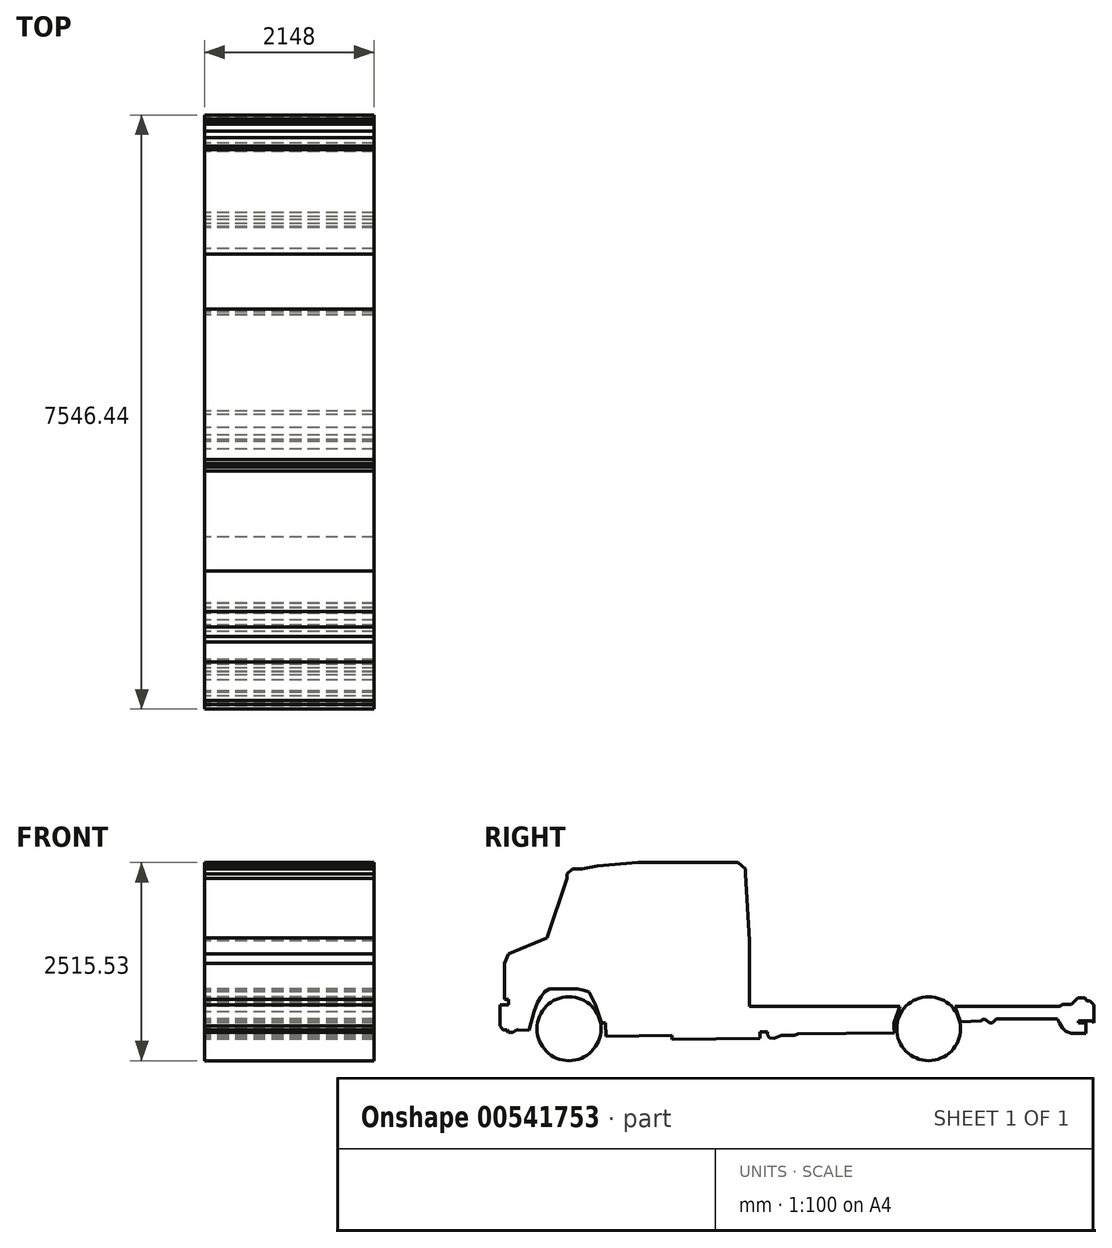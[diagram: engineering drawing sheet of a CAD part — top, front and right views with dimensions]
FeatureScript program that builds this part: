
annotation { "Feature Type Name" : "Feature", "Feature Type Description" : "" }
export const myFeature = defineFeature(function(context is Context, id is Id, definition is map)
    precondition{}
    {
        {
            var Q0;
            Q0=qCreatedBy(makeId("Right.planeOp"),FACE);
            var sketch = newSketch(context, id + "F0", { "sketchPlane" : qUnion([Q0])});
            skLineSegment(sketch, "E0", {"start": v(-5916.65, -35.76) * mm, "end": v(-5916.65, 86.1) * mm});
            skLineSegment(sketch, "E1", {"start": v(-5916.65, 86.1) * mm, "end": v(-5916.65, 228.27) * mm});
            skLineSegment(sketch, "E2", {"start": v(-5804.94, 228.27) * mm, "end": v(-5804.94, 299.36) * mm});
            skLineSegment(sketch, "E3", {"start": v(-5804.94, 299.36) * mm, "end": v(-5855.72, 299.36) * mm});
            skLineSegment(sketch, "E4", {"start": v(-5855.72, 299.36) * mm, "end": v(-5855.72, 664.94) * mm});
            skLineSegment(sketch, "E5", {"start": v(-5855.72, 664.94) * mm, "end": v(-5855.72, 756.33) * mm});
            skLineSegment(sketch, "E6", {"start": v(-5855.72, 756.33) * mm, "end": v(-5804.94, 878.2) * mm});
            skLineSegment(sketch, "E7", {"start": v(-5804.94, 878.2) * mm, "end": v(-5317.5, 1081.3) * mm});
            skLineSegment(sketch, "E8", {"start": v(-5317.5, 1081.3) * mm, "end": v(-5063.63, 1832.76) * mm});
            skLineSegment(sketch, "E9", {"start": v(-5063.63, 1832.76) * mm, "end": v(-5063.63, 1893.7) * mm});
            skLineSegment(sketch, "E10", {"start": v(-5063.63, 1893.7) * mm, "end": v(-4992.54, 1954.62) * mm});
            skLineSegment(sketch, "E11", {"start": v(-4992.54, 1954.62) * mm, "end": v(-4921.46, 1954.62) * mm});
            skLineSegment(sketch, "E12", {"start": v(-4921.46, 1954.62) * mm, "end": v(-4870.68, 1954.62) * mm});
            skLineSegment(sketch, "E13", {"start": v(-4870.68, 1954.62) * mm, "end": v(-4677.74, 1995.24) * mm});
            skLineSegment(sketch, "E14", {"start": v(-4677.74, 1995.24) * mm, "end": v(-4159.83, 2035.86) * mm});
            skLineSegment(sketch, "E15", {"start": v(-4159.83, 2035.86) * mm, "end": v(-2971.7, 2035.86) * mm});
            skLineSegment(sketch, "E16", {"start": v(-2971.7, 2035.86) * mm, "end": v(-2890.46, 2035.86) * mm});
            skLineSegment(sketch, "E17", {"start": v(-2890.46, 2035.86) * mm, "end": v(-2839.68, 1995.24) * mm});
            skLineSegment(sketch, "E18", {"start": v(-2839.68, 1995.24) * mm, "end": v(-2799.06, 1954.62) * mm});
            skLineSegment(sketch, "E19", {"start": v(-2799.06, 1954.62) * mm, "end": v(-2799.06, 1893.7) * mm});
            skLineSegment(sketch, "E20", {"start": v(-2799.06, 1893.7) * mm, "end": v(-2748.29, 1040.67) * mm});
            skLineSegment(sketch, "E21", {"start": v(-2748.29, 1040.67) * mm, "end": v(-2748.29, 675.1) * mm});
            skLineSegment(sketch, "E22", {"start": v(-2748.29, 675.1) * mm, "end": v(-2748.29, 228.27) * mm});
            skLineSegment(sketch, "E23", {"start": v(-2748.29, 228.27) * mm, "end": v(-2748.29, 210.87) * mm});
            skLineSegment(sketch, "E24", {"start": v(-2748.29, 210.87) * mm, "end": v(-832.65, 210.87) * mm});
            skLineSegment(sketch, "E25", {"start": v(-137.88, 210.87) * mm, "end": v(1193.96, 210.87) * mm});
            skLineSegment(sketch, "E26", {"start": v(1193.96, 210.87) * mm, "end": v(1235.52, 234.86) * mm});
            skLineSegment(sketch, "E27", {"start": v(1235.52, 234.86) * mm, "end": v(1346.42, 234.86) * mm});
            skLineSegment(sketch, "E28", {"start": v(1346.42, 234.86) * mm, "end": v(1427.07, 320.56) * mm});
            skLineSegment(sketch, "E29", {"start": v(1427.07, 320.56) * mm, "end": v(1512.77, 320.56) * mm});
            skLineSegment(sketch, "E30", {"start": v(1512.77, 320.56) * mm, "end": v(1543.24, 277.7) * mm});
            skPoint(sketch, "E30.endSnap0", {"position": v(1386.74, 277.7) * mm});
            skLineSegment(sketch, "E31", {"start": v(1543.24, 277.7) * mm, "end": v(1580.36, 277.7) * mm});
            skLineSegment(sketch, "E32", {"start": v(1580.36, 277.7) * mm, "end": v(1629.79, 231.19) * mm});
            skLineSegment(sketch, "E33", {"start": v(1629.79, 231.19) * mm, "end": v(1629.79, 210.87) * mm});
            skLineSegment(sketch, "E34", {"start": v(1629.79, 210.87) * mm, "end": v(1629.79, 0) * mm});
            skLineSegment(sketch, "E35", {"start": v(1629.79, 0) * mm, "end": v(1602.62, 25.56) * mm});
            skLineSegment(sketch, "E36", {"start": v(1602.62, 25.56) * mm, "end": v(1431.9, 25.56) * mm});
            skLineSegment(sketch, "E37", {"start": v(1431.9, 25.56) * mm, "end": v(1431.9, 0) * mm});
            skLineSegment(sketch, "E38", {"start": v(1431.9, 0) * mm, "end": v(1528.4, 0) * mm});
            skLineSegment(sketch, "E39", {"start": v(1528.4, 0) * mm, "end": v(1528.4, -130.55) * mm});
            skLineSegment(sketch, "E40", {"start": v(1528.4, -130.55) * mm, "end": v(1342.82, -130.55) * mm});
            skLineSegment(sketch, "E41", {"start": v(1342.82, -130.55) * mm, "end": v(1276, -104.57) * mm});
            skLineSegment(sketch, "E42", {"start": v(1276, -104.57) * mm, "end": v(1231.78, -62.95) * mm});
            skLineSegment(sketch, "E43", {"start": v(1231.78, -62.95) * mm, "end": v(1190.64, 0) * mm});
            skLineSegment(sketch, "E44", {"start": v(1190.64, 0) * mm, "end": v(1168.37, 51.32) * mm});
            skLineSegment(sketch, "E45", {"start": v(1168.37, 51.32) * mm, "end": v(388.94, 51.32) * mm});
            skLineSegment(sketch, "E46", {"start": v(388.94, 51.32) * mm, "end": v(364.7, 25.56) * mm});
            skLineSegment(sketch, "E47", {"start": v(364.7, 25.56) * mm, "end": v(340.64, 0) * mm});
            skLineSegment(sketch, "E48", {"start": v(340.64, 0) * mm, "end": v(299.86, 0) * mm});
            skLineSegment(sketch, "E49", {"start": v(299.86, 0) * mm, "end": v(254.57, 42.63) * mm});
            skLineSegment(sketch, "E50", {"start": v(254.57, 42.63) * mm, "end": v(214.5, 42.63) * mm});
            skLineSegment(sketch, "E51", {"start": v(214.5, 42.63) * mm, "end": v(198.43, 25.56) * mm});
            skLineSegment(sketch, "E52", {"start": v(198.43, 25.56) * mm, "end": v(-64.52, 14.99) * mm});
            skLineSegment(sketch, "E53", {"start": v(-912.82, -56.35) * mm, "end": v(-905.71, -124.93) * mm});
            skLineSegment(sketch, "E54", {"start": v(-905.71, -124.93) * mm, "end": v(-2131.69, -137.57) * mm});
            skLineSegment(sketch, "E55", {"start": v(-2131.69, -137.57) * mm, "end": v(-2172.13, -155.27) * mm});
            skLineSegment(sketch, "E56", {"start": v(-2172.13, -155.27) * mm, "end": v(-2217.63, -155.27) * mm});
            skLineSegment(sketch, "E57", {"start": v(-2217.63, -155.27) * mm, "end": v(-2339.05, -155.27) * mm});
            skLineSegment(sketch, "E58", {"start": v(-2339.05, -155.27) * mm, "end": v(-2437.5, -196.7) * mm});
            skLineSegment(sketch, "E59", {"start": v(-2437.5, -196.7) * mm, "end": v(-2493.39, -188.28) * mm});
            skLineSegment(sketch, "E60", {"start": v(-2493.39, -188.28) * mm, "end": v(-2516.89, -149.07) * mm});
            skLineSegment(sketch, "E61", {"start": v(-2516.89, -149.07) * mm, "end": v(-2517.25, -114.17) * mm});
            skLineSegment(sketch, "E62", {"start": v(-2517.25, -114.17) * mm, "end": v(-2612.21, -115.15) * mm});
            skLineSegment(sketch, "E63", {"start": v(-2612.21, -115.15) * mm, "end": v(-2611.37, -196.7) * mm});
            skLineSegment(sketch, "E64", {"start": v(-2611.37, -196.7) * mm, "end": v(-3726.8, -208.2) * mm});
            skLineSegment(sketch, "E65", {"start": v(-3726.8, -208.2) * mm, "end": v(-3727.3, -159.88) * mm});
            skLineSegment(sketch, "E66", {"start": v(-3727.3, -159.88) * mm, "end": v(-3906.21, -161.72) * mm});
            skLineSegment(sketch, "E67", {"start": v(-3906.21, -161.72) * mm, "end": v(-4569.7, -168.56) * mm});
            skLineSegment(sketch, "E68", {"start": v(-5684.27, -88.6) * mm, "end": v(-5704.27, -88.6) * mm});
            skLineSegment(sketch, "E69", {"start": v(-5704.27, -88.6) * mm, "end": v(-5748.28, -120.6) * mm});
            skLineSegment(sketch, "E70", {"start": v(-5748.28, -120.6) * mm, "end": v(-5808.3, -120.6) * mm});
            skLineSegment(sketch, "E71", {"start": v(-5808.3, -120.6) * mm, "end": v(-5828.3, -88.6) * mm});
            skLineSegment(sketch, "E72", {"start": v(-5828.3, -88.6) * mm, "end": v(-5876.32, -88.6) * mm});
            skLineSegment(sketch, "E73", {"start": v(-5876.32, -88.6) * mm, "end": v(-5916.65, -35.76) * mm});
            skLineSegment(sketch, "E74", {"start": v(-4569.7, -168.56) * mm, "end": v(-4571.43, 0) * mm});
            skLineSegment(sketch, "E75", {"start": v(-4571.43, 0) * mm, "end": v(-4626.28, -0.57) * mm});
            skLineSegment(sketch, "E76", {"start": v(-4626.28, -0.57) * mm, "end": v(-4698.56, 231.55) * mm});
            skLineSegment(sketch, "E77", {"start": v(-4698.56, 231.55) * mm, "end": v(-4784.7, 395.21) * mm});
            skLineSegment(sketch, "E78", {"start": v(-4784.7, 395.21) * mm, "end": v(-4845, 412.44) * mm});
            skLineSegment(sketch, "E79", {"start": v(-4845, 412.44) * mm, "end": v(-4931.13, 429.67) * mm});
            skLineSegment(sketch, "E80", {"start": v(-4931.13, 429.67) * mm, "end": v(-5288.6, 429.67) * mm});
            skLineSegment(sketch, "E81", {"start": v(-5288.6, 429.67) * mm, "end": v(-5348.89, 395.21) * mm});
            skLineSegment(sketch, "E82", {"start": v(-5348.89, 395.21) * mm, "end": v(-5396.26, 330.6) * mm});
            skLineSegment(sketch, "E83", {"start": v(-5396.26, 330.6) * mm, "end": v(-5435.03, 261.7) * mm});
            skLineSegment(sketch, "E84", {"start": v(-5435.03, 261.7) * mm, "end": v(-5482.4, 141.11) * mm});
            skLineSegment(sketch, "E85", {"start": v(-5482.4, 141.11) * mm, "end": v(-5521.16, 0) * mm});
            skLineSegment(sketch, "E86", {"start": v(-5521.16, 0) * mm, "end": v(-5547, -95.76) * mm});
            skLineSegment(sketch, "E87", {"start": v(-5547, -95.76) * mm, "end": v(-5684.27, -88.6) * mm});
            skLineSegment(sketch, "E88", {"start": v(-912.82, -56.35) * mm, "end": v(-912.82, 0) * mm});
            skLineSegment(sketch, "E89", {"start": v(-912.82, 0) * mm, "end": v(-832.65, 210.87) * mm});
            skLineSegment(sketch, "E90", {"start": v(-137.88, 210.87) * mm, "end": v(-64.52, 14.99) * mm});
            skLineSegment(sketch, "E91", {"start": v(-5057.04, -479.22) * mm, "end": v(-466.6, -479.22) * mm, "construction": true});
            skLineSegment(sketch, "E92", {"start": v(-5046.9, 331.86) * mm, "end": v(-474.37, 331.86) * mm, "construction": true});
            skLineSegment(sketch, "E93", {"start": v(-5916.65, 228.27) * mm, "end": v(-5804.94, 228.27) * mm});
            skLineSegment(sketch, "E94", {"start": v(-4632.78, -50.96) * mm, "end": v(-4632.78, 488.03) * mm, "construction": true});
            skLineSegment(sketch, "E95", {"start": v(-64.15, -93.56) * mm, "end": v(-64.15, 635.73) * mm, "construction": true});
            skSolve(sketch);
        }
        {
            var Q0;
            Q0=qCreatedBy(makeId("Right.planeOp"),FACE);
            var sketch = newSketch(context, id + "F1", { "sketchPlane" : qUnion([Q0])});
            skCircle(sketch, "E96", {"center": v(-5037.95, -73.86) * mm, "radius": 405.81 * mm});
            skPoint(sketch, "E96.first.point", {"position": v(-5046.9, 331.86) * mm});
            skPoint(sketch, "E96.second.point", {"position": v(-4632.78, -50.96) * mm});
            skPoint(sketch, "E96.third.point", {"position": v(-5057.04, -479.22) * mm});
            skCircle(sketch, "E97", {"center": v(-469.23, -73.67) * mm, "radius": 405.56 * mm});
            skPoint(sketch, "E97.first.point", {"position": v(-474.37, 331.86) * mm});
            skPoint(sketch, "E97.second.point", {"position": v(-64.15, -93.56) * mm});
            skPoint(sketch, "E97.third.point", {"position": v(-466.6, -479.22) * mm});
            skSolve(sketch);
        }
        {
            var Q0;
            Q0 = qSketchRegion(id + "F1", true);
            extrude(context, id + "F2", {"entities" : qUnion([Q0]), "depth" : 2148 * mm, "offsetDistance" : 25 * mm});
        }
        {
            var Q0;
            Q0 = qSketchRegion(id + "F0", true);
            extrude(context, id + "F3", {"entities" : qUnion([Q0]), "depth" : 2148 * mm, "offsetDistance" : 25 * mm});
        }
    });
